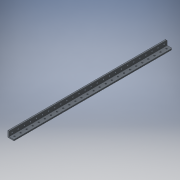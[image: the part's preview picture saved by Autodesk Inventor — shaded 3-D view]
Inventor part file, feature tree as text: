
AUTODESK INVENTOR PART (.ipt)
format: ipt  version: 2016 (Build 200138000, 138)  size: 259,584 bytes
history: native  units: in
note: dims shown in document units (in); Inventor stores cm internally (conversion verified against a paired STEP export)
features: other x40, sketch x4, hole x2, extrude x1
ambient origin geometry x8: Origin, YZ Plane, XZ Plane, XY Plane, X Axis, Y Axis, Z Axis, Center Point
bodies: Solid1 (feature_tree)
feature tree (47):
  other  "A_19"
  other  "A_20"
  other  "A_21"
  other  "A_22"
  other  "A_23"
  other  "A_24"
  other  "A_25"
  other  "A_26"
  other  "A_27"
  other  "A_37"
  other  "A_38"
  other  "A_39"
  other  "A_40"
  other  "A_41"
  other  "A_42"
  other  "A_43"
  other  "A_44"
  other  "A_45"
  other  "A_28"
  other  "A_29"
  other  "A_30"
  other  "A_31"
  other  "A_32"
  other  "A_33"
  other  "A_34"
  other  "A_35"
  other  "A_36"
  other  "A_46"
  other  "A_47"
  other  "A_48"
  other  "A_49"
  other  "A_50"
  other  "A_51"
  other  "A_52"
  other  "A_53"
  other  "A_54"
  other  "FRONT"
  other  "TOP"
  other  "RIGHT"
  extrude  "Extrusion1"  Depth=0.6299in
  hole  "Hole1"  [1 undecoded]
  sketch  "Sketch8"  dims[d5=0.6299in d6=0.6299in]
  hole  "Hole2"  [1 undecoded]
  sketch  "Sketch1"  dims[d0=5.0394in d1=0.0in d2=0.6299in]
  sketch  "Sketch7"  dims[d3=0.6299in d4=0.6299in]
  sketch  "Sketch9"  dims[d7=0.6299in d8=0.6299in d9=0.6299in d10=0.1457in d11=0.2362in d12=0.1575in d13=0.0787in d14=90.0deg d15=0.315in d16=0.8108in d17=0.6299in d18=0.6299in d19=0.6299in d20=0.6299in d21=0.6299in d22=0.6299in d23=0.6299in d24=0.6299in d25=0.1457in d26=0.2362in d27=0.1575in d28=0.0787in d29=90.0deg d30=0.315in d31=0.8108in]
  other  "tetrix_739071_2012"
note: 2 required parameter values undecoded (feature->parameter linkage not recoverable at this tier; creation-order binding heuristic only, values carry confidence <= 0.55)
